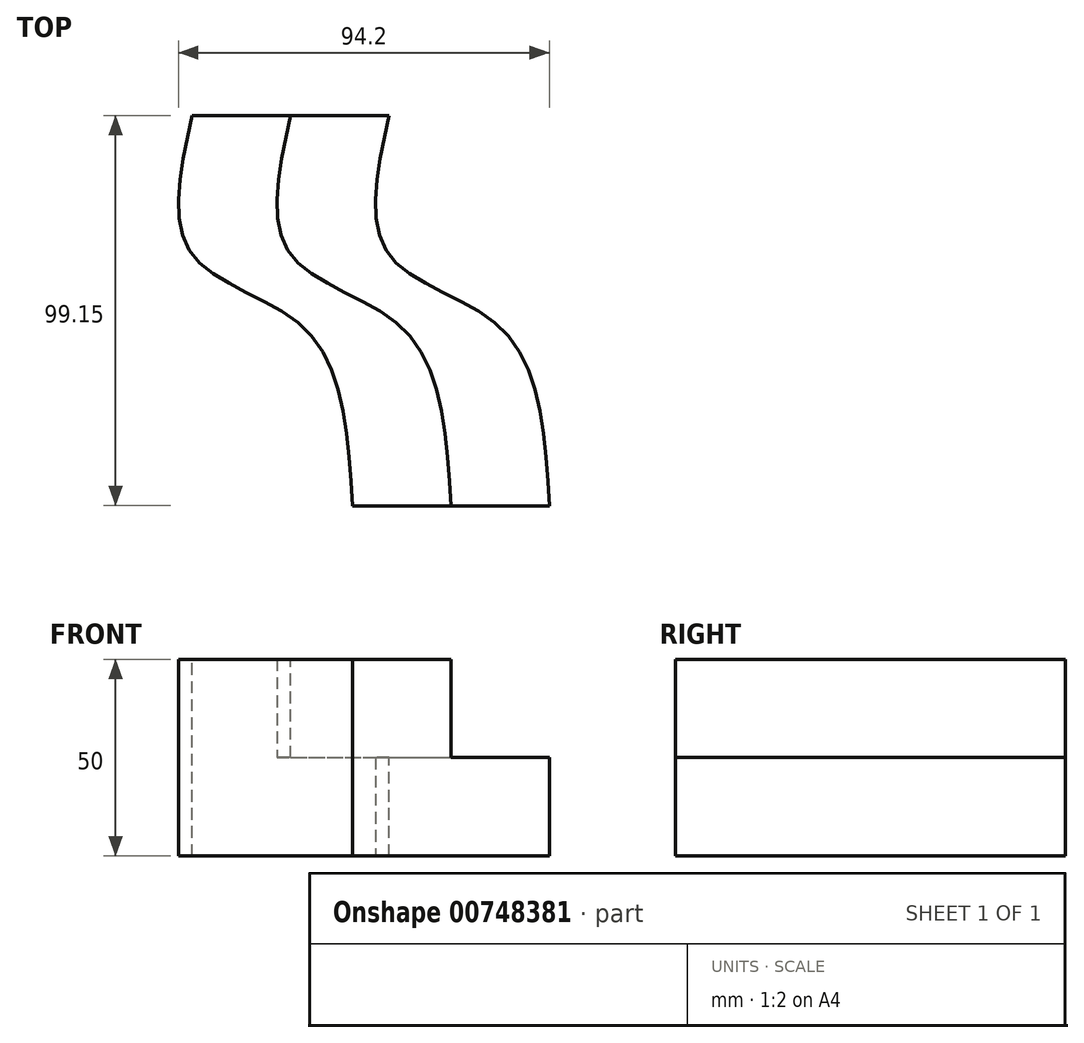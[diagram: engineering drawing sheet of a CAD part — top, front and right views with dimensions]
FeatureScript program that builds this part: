
annotation { "Feature Type Name" : "Feature", "Feature Type Description" : "" }
export const myFeature = defineFeature(function(context is Context, id is Id, definition is map)
    precondition{}
    {
        {
            var Q0;
            Q0=qCreatedBy(makeId("Front.planeOp"),FACE);
            var sketch = newSketch(context, id + "F0", { "sketchPlane" : qUnion([Q0])});
            skLineSegment(sketch, "E0.bottom", {"start": v(25, -25) * mm, "end": v(-25, -25) * mm});
            skLineSegment(sketch, "E0.top", {"start": v(0, 25) * mm, "end": v(-25, 25) * mm});
            skLineSegment(sketch, "E0.left", {"start": v(25, -25) * mm, "end": v(25, 0) * mm});
            skLineSegment(sketch, "E0.right", {"start": v(-25, -25) * mm, "end": v(-25, 25) * mm});
            skPoint(sketch, "E0.middle", {"position": v(0, 0) * mm});
            skLineSegment(sketch, "E1", {"start": v(0, 0) * mm, "end": v(0, 25) * mm});
            skLineSegment(sketch, "E2", {"start": v(0, 0) * mm, "end": v(25, 0) * mm});
            skPoint(sketch, "E3.orphan", {"position": v(25, 25) * mm});
            skSolve(sketch);
        }
        {
            var Q0;
            Q0=qCreatedBy(makeId("Top.planeOp"),FACE);
            var sketch = newSketch(context, id + "F1", { "sketchPlane" : qUnion([Q0])});
            skFitSpline(sketch, "E4", {"points": [v(0, 0) * mm, v(0, -35.37) * mm, v(29.15, -54.73) * mm, v(40.74, -99.15) * mm], "startDerivative": vector(-28.16, -127.9) * mm, "endDerivative": vector(8.37, -143.07) * mm});
            skSolve(sketch);
        }
        {
            var Q0;
            Q0=makeQuery(id+"F0.imprint","IMPRINT",FACE,{"disambiguationData":[TD([[makeQuery(id+"F0.imprint","IMPRINT",EDGE,{"derivedFrom":sQuery(id+"F0.wireOp",EDGE,"E0.bottom")}),-1.0]])]});
            var Q1;
            Q1=sQuery(id+"F1.wireOp",EDGE,"E4");
            sweep(context, id + "F2", {"profiles" : qUnion([Q0]), "path" : qUnion([Q1]), "keepProfileOrientation" : true});
        }
    });
